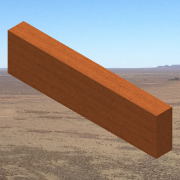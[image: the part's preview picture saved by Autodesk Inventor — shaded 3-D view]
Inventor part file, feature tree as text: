
AUTODESK INVENTOR PART (.ipt)
format: ipt  version: 2014 SP1 (Build 180222100, 222)  size: 126,464 bytes
history: native  units: in
note: dims shown in document units (in); Inventor stores cm internally (conversion verified against a paired STEP export)
features: extrude x1, sketch x1
ambient origin geometry x8: Origin, YZ Plane, XZ Plane, XY Plane, X Axis, Y Axis, Z Axis, Center Point
bodies: Solid1 (feature_tree)
feature tree (2):
  extrude  "Extrusion1"  Depth=3.5in
  sketch  "Sketch1"  dims[d0=1.5in d1=3.5in d2=14.0in d3=0.0in]
